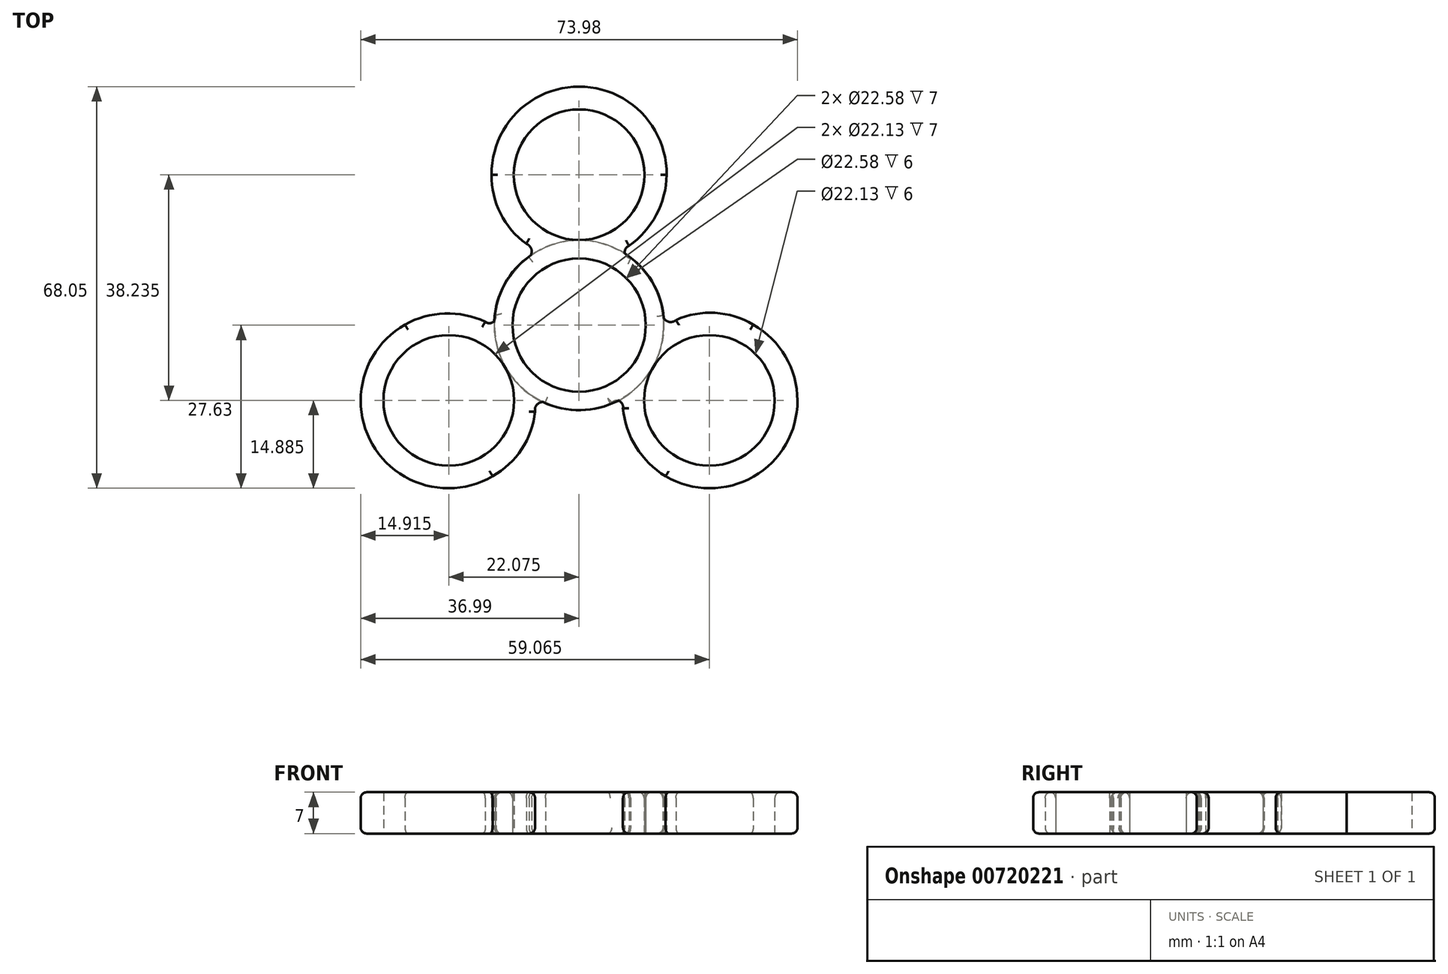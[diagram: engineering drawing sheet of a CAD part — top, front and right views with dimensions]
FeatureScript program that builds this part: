
annotation { "Feature Type Name" : "Feature", "Feature Type Description" : "" }
export const myFeature = defineFeature(function(context is Context, id is Id, definition is map)
    precondition{}
    {
        {
            var Q0;
            Q0=qCreatedBy(makeId("Top.planeOp"),FACE);
            var sketch = newSketch(context, id + "F0", { "sketchPlane" : qUnion([Q0])});
            skCircle(sketch, "E0", {"center": v(0, 0) * mm, "radius": 11.29 * mm});
            skCircle(sketch, "E1", {"center": v(0, 25.5) * mm, "radius": 11.07 * mm});
            skArc(sketch, "E2", {"start": v(14.84, 25.5) * mm, "mid": v(0, 40.42) * mm, "end": v(-14.84, 25.5) * mm});
            skArc(sketch, "E3", {"start": v(-8.49, 11.49) * mm, "mid": v(-8.06, 12.76) * mm, "end": v(-8.95, 13.78) * mm});
            skArc(sketch, "E4", {"start": v(8.45, 13.46) * mm, "mid": v(7.74, 12.29) * mm, "end": v(8.7, 11.32) * mm});
            skArc(sketch, "E5", {"start": v(-8.49, 11.49) * mm, "mid": v(-0.14, -14.4) * mm, "end": v(8.7, 11.32) * mm});
            skArc(sketch, "E6", {"start": v(-14.84, 25.5) * mm, "mid": v(-13.32, 18.91) * mm, "end": v(-8.95, 13.78) * mm});
            skArc(sketch, "E7", {"start": v(8.45, 13.46) * mm, "mid": v(13.08, 18.7) * mm, "end": v(14.84, 25.5) * mm});
            skSolve(sketch);
        }
        {
            var Q0;
            Q0 = qSketchRegion(id + "F0", true);
            extrude(context, id + "F1", {"entities" : qUnion([Q0]), "depth" : 7 * mm, "offsetDistance" : 25 * mm});
        }
        {
            var Q0;
            Q0=qCreatedBy(makeId("Right.planeOp"),FACE);
            var sketch = newSketch(context, id + "F2", { "sketchPlane" : qUnion([Q0])});
            skLineSegment(sketch, "E8", {"start": v(0, 57.03) * mm, "end": v(0, -50.46) * mm});
            skSolve(sketch);
        }
        {
            var Q0;
            Q0=makeQuery(id+"F1.opExtrude","SWEPT_BODY",BODY,{"disambiguationData":[OSD([sQuery(id+"F0.wireOp",EDGE,"E0"),sQuery(id+"F0.wireOp",EDGE,"E1"),sQuery(id+"F0.wireOp",EDGE,"E2"),sQuery(id+"F0.wireOp",EDGE,"E3"),sQuery(id+"F0.wireOp",EDGE,"E4"),sQuery(id+"F0.wireOp",EDGE,"E5"),sQuery(id+"F0.wireOp",EDGE,"E6"),sQuery(id+"F0.wireOp",EDGE,"E7")])]});
            var Q1;
            Q1=sQuery(id+"F2.wireOp",EDGE,"E8");
            circularPattern(context, id + "F3", {"entities" : qUnion([Q0]), "axis" : qUnion([Q1]), "angle" : 360 * degree, "instanceCount" : 3, "equalSpace" : true});
        }
        {
            var Q0;
            Q0=makeQuery(id+"F3.opPattern","COPY",EDGE,{"derivedFrom":makeQuery(id+"F1.opExtrude","CAP_EDGE",EDGE,{"disambiguationData":[OSD([sQuery(id+"F0.wireOp",EDGE,"E6")])],"isStart":false}),"instanceName":"2"});
            var Q1;
            Q1=makeQuery(id+"F3.opPattern","COPY",EDGE,{"derivedFrom":makeQuery(id+"F1.opExtrude","CAP_EDGE",EDGE,{"disambiguationData":[OSD([sQuery(id+"F0.wireOp",EDGE,"E2")])],"isStart":false}),"instanceName":"2"});
            var Q2;
            Q2=makeQuery(id+"F3.opPattern","COPY",EDGE,{"derivedFrom":makeQuery(id+"F1.opExtrude","CAP_EDGE",EDGE,{"disambiguationData":[OSD([sQuery(id+"F0.wireOp",EDGE,"E7")])],"isStart":false}),"instanceName":"2"});
            var Q3;
            Q3=makeQuery(id+"F3.opPattern","COPY",EDGE,{"derivedFrom":makeQuery(id+"F1.opExtrude","CAP_EDGE",EDGE,{"disambiguationData":[OSD([sQuery(id+"F0.wireOp",EDGE,"E4")])],"isStart":false}),"instanceName":"2"});
            var Q4;
            Q4=makeQuery(id+"F3.opPattern","COPY",EDGE,{"derivedFrom":makeQuery(id+"F1.opExtrude","CAP_EDGE",EDGE,{"disambiguationData":[OSD([sQuery(id+"F0.wireOp",EDGE,"E3")])],"isStart":false}),"instanceName":"2"});
            var Q5;
            Q5=makeQuery(id+"F3.opPattern","COPY",EDGE,{"derivedFrom":makeQuery(id+"F1.opExtrude","CAP_EDGE",EDGE,{"disambiguationData":[OSD([sQuery(id+"F0.wireOp",EDGE,"E4")])],"isStart":false}),"instanceName":"1"});
            var Q6;
            Q6=makeQuery(id+"F3.opPattern","COPY",EDGE,{"derivedFrom":makeQuery(id+"F1.opExtrude","CAP_EDGE",EDGE,{"disambiguationData":[OSD([sQuery(id+"F0.wireOp",EDGE,"E7")])],"isStart":false}),"instanceName":"1"});
            var Q7;
            Q7=makeQuery(id+"F3.opPattern","COPY",EDGE,{"derivedFrom":makeQuery(id+"F1.opExtrude","CAP_EDGE",EDGE,{"disambiguationData":[OSD([sQuery(id+"F0.wireOp",EDGE,"E2")])],"isStart":false}),"instanceName":"1"});
            var Q8;
            Q8=makeQuery(id+"F3.opPattern","COPY",EDGE,{"derivedFrom":makeQuery(id+"F1.opExtrude","CAP_EDGE",EDGE,{"disambiguationData":[OSD([sQuery(id+"F0.wireOp",EDGE,"E6")])],"isStart":false}),"instanceName":"1"});
            var Q9;
            Q9=makeQuery(id+"F3.opPattern","COPY",FACE,{"derivedFrom":makeQuery(id+"F1.opExtrude","CAP_FACE",FACE,{"disambiguationData":[OSD([sQuery(id+"F0.wireOp",EDGE,"E0"),sQuery(id+"F0.wireOp",EDGE,"E1"),sQuery(id+"F0.wireOp",EDGE,"E2"),sQuery(id+"F0.wireOp",EDGE,"E3"),sQuery(id+"F0.wireOp",EDGE,"E4"),sQuery(id+"F0.wireOp",EDGE,"E5"),sQuery(id+"F0.wireOp",EDGE,"E6"),sQuery(id+"F0.wireOp",EDGE,"E7")])],"isStart":false}),"instanceName":"1"});
            var Q10;
            Q10=makeQuery(id+"F1.opExtrude","CAP_EDGE",EDGE,{"disambiguationData":[OSD([sQuery(id+"F0.wireOp",EDGE,"E6")])],"isStart":false});
            var Q11;
            Q11=makeQuery(id+"F1.opExtrude","CAP_EDGE",EDGE,{"disambiguationData":[OSD([sQuery(id+"F0.wireOp",EDGE,"E3")])],"isStart":false});
            var Q12;
            Q12=makeQuery(id+"F1.opExtrude","CAP_EDGE",EDGE,{"disambiguationData":[OSD([sQuery(id+"F0.wireOp",EDGE,"E4")])],"isStart":false});
            var Q13;
            Q13=makeQuery(id+"F1.opExtrude","CAP_EDGE",EDGE,{"disambiguationData":[OSD([sQuery(id+"F0.wireOp",EDGE,"E7")])],"isStart":false});
            var Q14;
            Q14=makeQuery(id+"F1.opExtrude","CAP_EDGE",EDGE,{"disambiguationData":[OSD([sQuery(id+"F0.wireOp",EDGE,"E5")])],"isStart":false});
            var Q15;
            Q15=makeQuery(id+"F3.opPattern","COPY",EDGE,{"derivedFrom":makeQuery(id+"F1.opExtrude","CAP_EDGE",EDGE,{"disambiguationData":[OSD([sQuery(id+"F0.wireOp",EDGE,"E5")])],"isStart":false}),"instanceName":"1"});
            fillet(context, id + "F4", {"entities" : qUnion([Q0, Q1, Q2, Q3, Q4, Q5, Q6, Q7, Q8, Q9, Q10, Q11, Q12, Q13, Q14, Q15]), "radius" : 1 * mm, "tangentPropagation" : true, "allowEdgeOverflow" : false});
        }
        {
            var Q0;
            Q0=makeQuery(id+"F3.opPattern","COPY",EDGE,{"derivedFrom":makeQuery(id+"F1.opExtrude","CAP_EDGE",EDGE,{"disambiguationData":[OSD([sQuery(id+"F0.wireOp",EDGE,"E5")])],"isStart":false}),"instanceName":"2"});
            var Q1;
            Q1=makeQuery(id+"F3.opPattern","COPY",EDGE,{"derivedFrom":makeQuery(id+"F1.opExtrude","CAP_EDGE",EDGE,{"disambiguationData":[OSD([sQuery(id+"F0.wireOp",EDGE,"E6")])],"isStart":true}),"instanceName":"1"});
            var Q2;
            Q2=makeQuery(id+"F3.opPattern","COPY",EDGE,{"derivedFrom":makeQuery(id+"F1.opExtrude","CAP_EDGE",EDGE,{"disambiguationData":[OSD([sQuery(id+"F0.wireOp",EDGE,"E2")])],"isStart":true}),"instanceName":"1"});
            var Q3;
            Q3=makeQuery(id+"F3.opPattern","COPY",EDGE,{"derivedFrom":makeQuery(id+"F1.opExtrude","CAP_EDGE",EDGE,{"disambiguationData":[OSD([sQuery(id+"F0.wireOp",EDGE,"E7")])],"isStart":true}),"instanceName":"1"});
            var Q4;
            Q4=makeQuery(id+"F3.opPattern","COPY",EDGE,{"derivedFrom":makeQuery(id+"F1.opExtrude","CAP_EDGE",EDGE,{"disambiguationData":[OSD([sQuery(id+"F0.wireOp",EDGE,"E4")])],"isStart":true}),"instanceName":"1"});
            var Q5;
            Q5=makeQuery(id+"F3.opPattern","COPY",EDGE,{"derivedFrom":makeQuery(id+"F1.opExtrude","CAP_EDGE",EDGE,{"disambiguationData":[OSD([sQuery(id+"F0.wireOp",EDGE,"E3")])],"isStart":true}),"instanceName":"2"});
            var Q6;
            Q6=makeQuery(id+"F3.opPattern","COPY",EDGE,{"derivedFrom":makeQuery(id+"F1.opExtrude","CAP_EDGE",EDGE,{"disambiguationData":[OSD([sQuery(id+"F0.wireOp",EDGE,"E6")])],"isStart":true}),"instanceName":"2"});
            var Q7;
            Q7=makeQuery(id+"F3.opPattern","COPY",EDGE,{"derivedFrom":makeQuery(id+"F1.opExtrude","CAP_EDGE",EDGE,{"disambiguationData":[OSD([sQuery(id+"F0.wireOp",EDGE,"E2")])],"isStart":true}),"instanceName":"2"});
            var Q8;
            Q8=makeQuery(id+"F3.opPattern","COPY",EDGE,{"derivedFrom":makeQuery(id+"F1.opExtrude","CAP_EDGE",EDGE,{"disambiguationData":[OSD([sQuery(id+"F0.wireOp",EDGE,"E7")])],"isStart":true}),"instanceName":"2"});
            var Q9;
            Q9=makeQuery(id+"F1.opExtrude","CAP_EDGE",EDGE,{"disambiguationData":[OSD([sQuery(id+"F0.wireOp",EDGE,"E6")])],"isStart":true});
            var Q10;
            Q10=makeQuery(id+"F1.opExtrude","CAP_EDGE",EDGE,{"disambiguationData":[OSD([sQuery(id+"F0.wireOp",EDGE,"E3")])],"isStart":true});
            var Q11;
            Q11=makeQuery(id+"F1.opExtrude","CAP_EDGE",EDGE,{"disambiguationData":[OSD([sQuery(id+"F0.wireOp",EDGE,"E2")])],"isStart":true});
            var Q12;
            Q12=makeQuery(id+"F1.opExtrude","CAP_EDGE",EDGE,{"disambiguationData":[OSD([sQuery(id+"F0.wireOp",EDGE,"E7")])],"isStart":true});
            var Q13;
            Q13=makeQuery(id+"F1.opExtrude","CAP_EDGE",EDGE,{"disambiguationData":[OSD([sQuery(id+"F0.wireOp",EDGE,"E4")])],"isStart":true});
            var Q14;
            Q14=makeQuery(id+"F3.opPattern","COPY",EDGE,{"derivedFrom":makeQuery(id+"F1.opExtrude","CAP_EDGE",EDGE,{"disambiguationData":[OSD([sQuery(id+"F0.wireOp",EDGE,"E3")])],"isStart":true}),"instanceName":"1"});
            var Q15;
            Q15=makeQuery(id+"F1.opExtrude","CAP_EDGE",EDGE,{"disambiguationData":[OSD([sQuery(id+"F0.wireOp",EDGE,"E5")])],"isStart":true});
            var Q16;
            Q16=makeQuery(id+"F3.opPattern","COPY",EDGE,{"derivedFrom":makeQuery(id+"F1.opExtrude","CAP_EDGE",EDGE,{"disambiguationData":[OSD([sQuery(id+"F0.wireOp",EDGE,"E4")])],"isStart":true}),"instanceName":"2"});
            fillet(context, id + "F5", {"entities" : qUnion([Q0, Q1, Q2, Q3, Q4, Q5, Q6, Q7, Q8, Q9, Q10, Q11, Q12, Q13, Q14, Q15, Q16]), "radius" : 1 * mm, "tangentPropagation" : true, "allowEdgeOverflow" : false});
        }
        {
            var Q0;
            Q0=makeQuery(id+"F3.opPattern","COPY",EDGE,{"derivedFrom":makeQuery(id+"F1.opExtrude","CAP_EDGE",EDGE,{"disambiguationData":[OSD([sQuery(id+"F0.wireOp",EDGE,"E2")])],"isStart":true}),"instanceName":"2"});
            var Q1;
            Q1=makeQuery(id+"F3.opPattern","COPY",EDGE,{"derivedFrom":makeQuery(id+"F1.opExtrude","CAP_EDGE",EDGE,{"disambiguationData":[OSD([sQuery(id+"F0.wireOp",EDGE,"E6")])],"isStart":true}),"instanceName":"2"});
            var Q2;
            Q2=makeQuery(id+"F3.opPattern","COPY",EDGE,{"derivedFrom":makeQuery(id+"F1.opExtrude","CAP_EDGE",EDGE,{"disambiguationData":[OSD([sQuery(id+"F0.wireOp",EDGE,"E3")])],"isStart":true}),"instanceName":"2"});
            var Q3;
            Q3=makeQuery(id+"F3.opPattern","COPY",EDGE,{"derivedFrom":makeQuery(id+"F1.opExtrude","CAP_EDGE",EDGE,{"disambiguationData":[OSD([sQuery(id+"F0.wireOp",EDGE,"E5")])],"isStart":true}),"instanceName":"1"});
            var Q4;
            Q4=makeQuery(id+"F3.opPattern","COPY",EDGE,{"derivedFrom":makeQuery(id+"F1.opExtrude","CAP_EDGE",EDGE,{"disambiguationData":[OSD([sQuery(id+"F0.wireOp",EDGE,"E4")])],"isStart":true}),"instanceName":"1"});
            var Q5;
            Q5=makeQuery(id+"F3.opPattern","COPY",EDGE,{"derivedFrom":makeQuery(id+"F1.opExtrude","CAP_EDGE",EDGE,{"disambiguationData":[OSD([sQuery(id+"F0.wireOp",EDGE,"E7")])],"isStart":true}),"instanceName":"1"});
            var Q6;
            Q6=makeQuery(id+"F1.opExtrude","CAP_EDGE",EDGE,{"disambiguationData":[OSD([sQuery(id+"F0.wireOp",EDGE,"E5")])],"isStart":true});
            var Q7;
            Q7=makeQuery(id+"F3.opPattern","COPY",EDGE,{"derivedFrom":makeQuery(id+"F1.opExtrude","CAP_EDGE",EDGE,{"disambiguationData":[OSD([sQuery(id+"F0.wireOp",EDGE,"E2")])],"isStart":true}),"instanceName":"1"});
            var Q8;
            Q8=makeQuery(id+"F3.opPattern","COPY",EDGE,{"derivedFrom":makeQuery(id+"F1.opExtrude","CAP_EDGE",EDGE,{"disambiguationData":[OSD([sQuery(id+"F0.wireOp",EDGE,"E6")])],"isStart":true}),"instanceName":"1"});
            var Q9;
            Q9=makeQuery(id+"F3.opPattern","COPY",EDGE,{"derivedFrom":makeQuery(id+"F1.opExtrude","CAP_EDGE",EDGE,{"disambiguationData":[OSD([sQuery(id+"F0.wireOp",EDGE,"E3")])],"isStart":true}),"instanceName":"1"});
            var Q10;
            Q10=makeQuery(id+"F1.opExtrude","CAP_EDGE",EDGE,{"disambiguationData":[OSD([sQuery(id+"F0.wireOp",EDGE,"E7")])],"isStart":true});
            var Q11;
            Q11=makeQuery(id+"F1.opExtrude","CAP_EDGE",EDGE,{"disambiguationData":[OSD([sQuery(id+"F0.wireOp",EDGE,"E4")])],"isStart":true});
            var Q12;
            Q12=makeQuery(id+"F1.opExtrude","CAP_EDGE",EDGE,{"disambiguationData":[OSD([sQuery(id+"F0.wireOp",EDGE,"E2")])],"isStart":true});
            var Q13;
            Q13=makeQuery(id+"F1.opExtrude","CAP_EDGE",EDGE,{"disambiguationData":[OSD([sQuery(id+"F0.wireOp",EDGE,"E6")])],"isStart":true});
            var Q14;
            Q14=makeQuery(id+"F1.opExtrude","CAP_EDGE",EDGE,{"disambiguationData":[OSD([sQuery(id+"F0.wireOp",EDGE,"E3")])],"isStart":true});
            var Q15;
            Q15=makeQuery(id+"F3.opPattern","COPY",EDGE,{"derivedFrom":makeQuery(id+"F1.opExtrude","CAP_EDGE",EDGE,{"disambiguationData":[OSD([sQuery(id+"F0.wireOp",EDGE,"E7")])],"isStart":true}),"instanceName":"2"});
            var Q16;
            Q16=makeQuery(id+"F3.opPattern","COPY",EDGE,{"derivedFrom":makeQuery(id+"F1.opExtrude","CAP_EDGE",EDGE,{"disambiguationData":[OSD([sQuery(id+"F0.wireOp",EDGE,"E4")])],"isStart":true}),"instanceName":"2"});
            fillet(context, id + "F6", {"entities" : qUnion([Q0, Q1, Q2, Q3, Q4, Q5, Q6, Q7, Q8, Q9, Q10, Q11, Q12, Q13, Q14, Q15, Q16]), "radius" : 1 * mm, "tangentPropagation" : true, "allowEdgeOverflow" : false});
        }
        {
            var Q0;
            Q0=makeQuery(id+"F3.opPattern","COPY",EDGE,{"derivedFrom":makeQuery(id+"F1.opExtrude","CAP_EDGE",EDGE,{"disambiguationData":[OSD([sQuery(id+"F0.wireOp",EDGE,"E5")])],"isStart":true}),"instanceName":"2"});
            fillet(context, id + "F7", {"entities" : qUnion([Q0]), "radius" : 1 * mm, "tangentPropagation" : true, "allowEdgeOverflow" : false});
        }
    });
